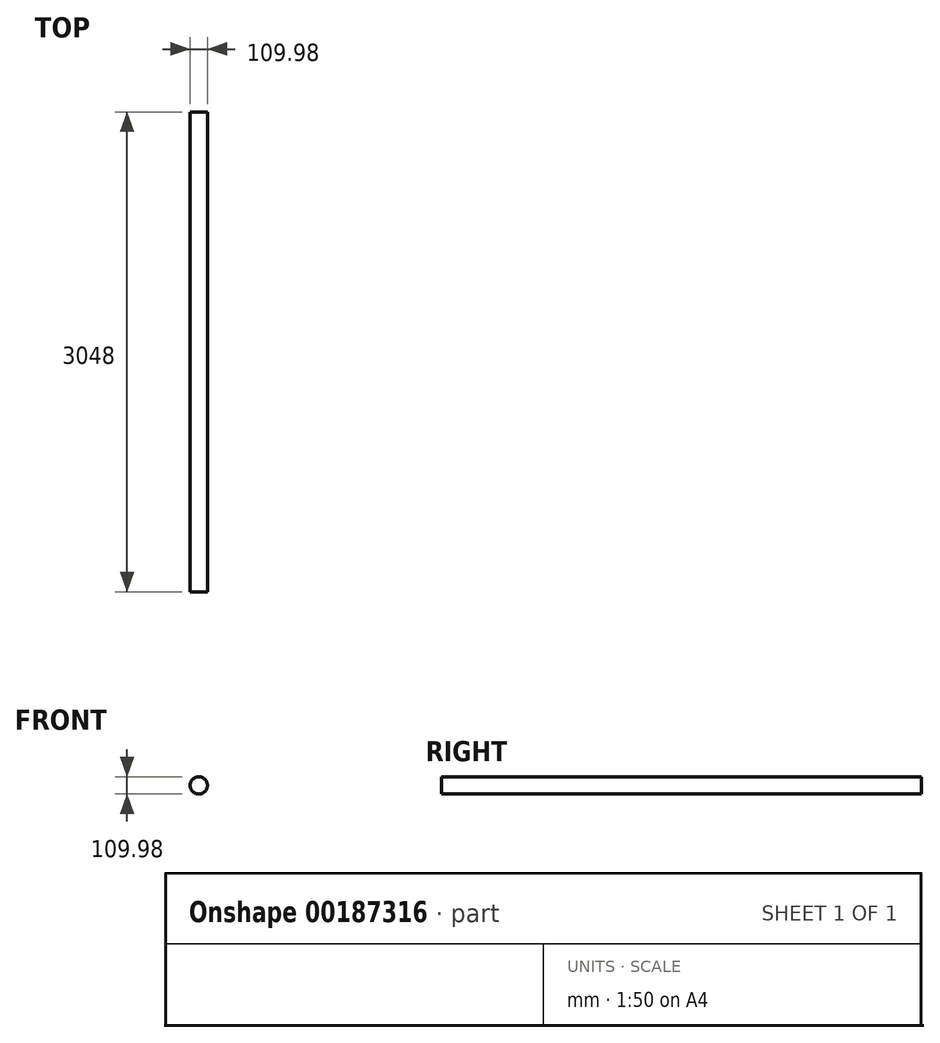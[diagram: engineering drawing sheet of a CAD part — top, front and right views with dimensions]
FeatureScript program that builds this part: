
annotation { "Feature Type Name" : "Feature", "Feature Type Description" : "" }
export const myFeature = defineFeature(function(context is Context, id is Id, definition is map)
    precondition{}
    {
        {
            var Q0;
            Q0=qCreatedBy(makeId("Front.planeOp"),FACE);
            var sketch = newSketch(context, id + "F0", { "sketchPlane" : qUnion([Q0])});
            skCircle(sketch, "E0", {"center": v(0, 0) * mm, "radius": 54.98 * mm});
            skSolve(sketch);
        }
        {
            var Q0;
            Q0 = qSketchRegion(id + "F0", true);
            extrude(context, id + "F1", {"entities" : qUnion([Q0]), "depth" : 3048 * mm});
        }
    });
